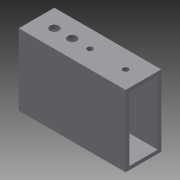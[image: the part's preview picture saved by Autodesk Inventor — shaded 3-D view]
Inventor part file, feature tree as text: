
AUTODESK INVENTOR PART (.ipt)
format: ipt  version: 2015 SP1 (Build 190203100, 203)  size: 114,688 bytes
history: native  units: in
note: dims shown in document units (in); Inventor stores cm internally (conversion verified against a paired STEP export)
features: sketch x3, extrude x2, projected_geometry x2, hole x1
ambient origin geometry x8: Origin, YZ Plane, XZ Plane, XY Plane, X Axis, Y Axis, Z Axis, Center Point
bodies: Solid1 (feature_tree)
feature tree (8):
  extrude  "Extrusion1"  Depth=1.0in
  hole  "Hole1"  [1 undecoded]
  extrude  "Extrusion3"  Depth=0.1in
  sketch  "Sketch1"  dims[d0=2.0in d1=1.0in]
  sketch  "Sketch2"  dims[d2=1.8in d3=0.8in]
  projected_geometry  "Projected Loop1"
  sketch  "Sketch4"  dims[d4=0.1in d5=0.1in d6=3.0in d7=0.0in d8=0.5in d9=0.5in d10=0.5in d11=0.5in d12=1.5in d13=2.5in d14=0.1562in d15=0.75in d16=0.375in d17=0.25in d18=0.5635in d19=1.0in d20=0.8108in d25=0.5in d26=1.0in d27=0.25in d28=0.25in d29=2.0in d30=0.0in]
  projected_geometry  "Projected Loop3"
note: 1 required parameter value undecoded (feature->parameter linkage not recoverable at this tier; creation-order binding heuristic only, values carry confidence <= 0.55)
